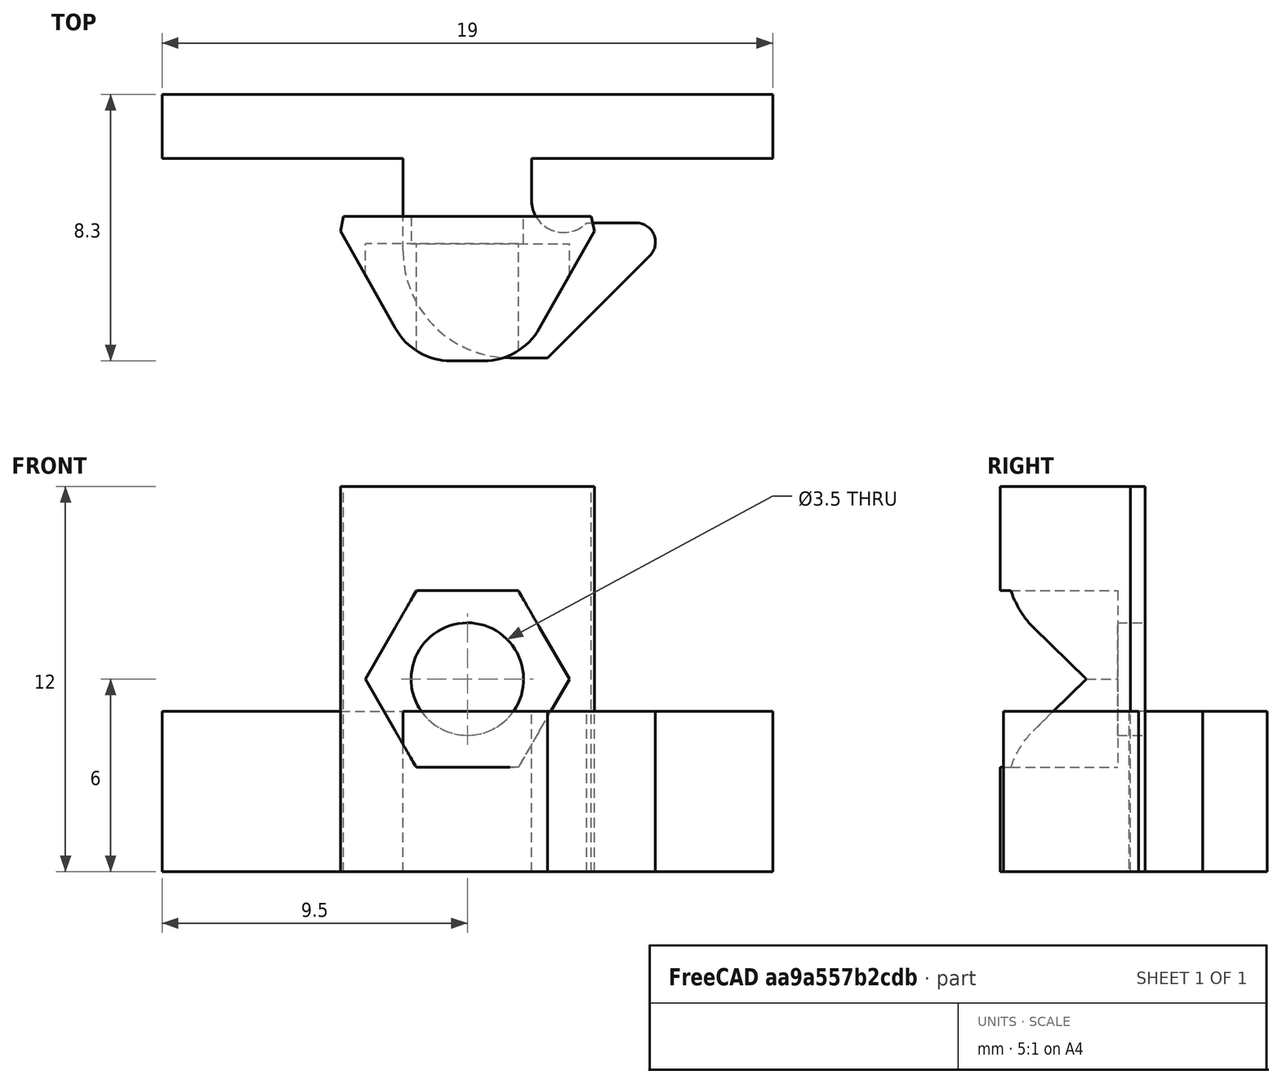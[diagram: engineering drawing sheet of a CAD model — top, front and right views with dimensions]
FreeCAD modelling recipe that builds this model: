
FCSTD DOCUMENT  (FreeCAD 0.18R)
Label: ISP5-3DP-T-Nut
Comment: Item Compatible Profile\nLook for ISP5-L20
License: All rights reserved
LicenseURL: http://en.wikipedia.org/wiki/All_rights_reserved
objects: Sketcher::SketchObject×6, PartDesign::Body×4, PartDesign::Pad×2, PartDesign::Pocket×2, Mesh::Feature×1
note: 18 computed .brp shape members not serialized (recipe doc carries the construction recipe); baked Part::Feature solids carry a one-line shape summary decoded from their .brp

FEATURE [Sketcher::SketchObject] CopySketch029  label="ISP5-L20-Profile"
  MapMode = 5
  sketch-geometry (70):
    g0: LineSegment StartX=-2.5 StartY=3.5 StartZ=0 EndX=-5.91967 EndY=6.91967 EndZ=0
    g1: LineSegment StartX=-5.38934 StartY=8.2 StartZ=0 EndX=-2.85 EndY=8.2 EndZ=0
    g2: LineSegment StartX=-3.35 StartY=10 StartZ=0 EndX=-8 EndY=10 EndZ=0
    g3: LineSegment StartX=-10 StartY=8 StartZ=0 EndX=-10 EndY=3.35 EndZ=0
    g4: LineSegment StartX=-9.25 StartY=2.6 StartZ=0 EndX=-8.45 EndY=2.6 EndZ=0
    g5: LineSegment StartX=-8.2 StartY=2.85 StartZ=0 EndX=-8.2 EndY=5.38934 EndZ=0
    g6: LineSegment StartX=-6.91967 StartY=5.91967 StartZ=0 EndX=-3.5 EndY=2.5 EndZ=0
    g7: LineSegment StartX=-2.6 StartY=9.25 StartZ=0 EndX=-2.6 EndY=8.45 EndZ=0
    g8: ArcOfCircle CenterX=-8 CenterY=8 CenterZ=0 NormalX=0 NormalY=0 NormalZ=1 AngleXU=0 Radius=2 StartAngle=1.5708 EndAngle=3.14159
    g9: ArcOfCircle CenterX=-3.35 CenterY=9.25 CenterZ=0 NormalX=0 NormalY=0 NormalZ=1 AngleXU=0 Radius=0.75 StartAngle=6e-16 EndAngle=1.5708
    g10: ArcOfCircle CenterX=-9.25 CenterY=3.35 CenterZ=0 NormalX=0 NormalY=0 NormalZ=1 AngleXU=0 Radius=0.75 StartAngle=3.14159 EndAngle=4.71239
    g11: ArcOfCircle CenterX=-5.38934 CenterY=7.45 CenterZ=0 NormalX=0 NormalY=0 NormalZ=1 AngleXU=0 Radius=0.75 StartAngle=1.5708 EndAngle=3.92699
    g12: ArcOfCircle CenterX=-7.45 CenterY=5.38934 CenterZ=0 NormalX=0 NormalY=0 NormalZ=1 AngleXU=0 Radius=0.75 StartAngle=0.785398 EndAngle=3.14159
    g13: LineSegment [constr] StartX=-5.38934 StartY=7.45 StartZ=0 EndX=-7.45 EndY=5.38934 EndZ=0
    g14: ArcOfCircle CenterX=-2.85 CenterY=8.45 CenterZ=0 NormalX=0 NormalY=0 NormalZ=1 AngleXU=0 Radius=0.25 StartAngle=4.71239 EndAngle=6.28319
    g15: Circle CenterX=0 CenterY=0 CenterZ=0 NormalX=0 NormalY=0 NormalZ=1 AngleXU=0 Radius=2.15
    g16: LineSegment StartX=2.5 StartY=3.5 StartZ=0 EndX=5.91967 EndY=6.91967 EndZ=0
    g17: LineSegment StartX=3.5 StartY=-2.5 StartZ=0 EndX=6.91967 EndY=-5.91967 EndZ=0
    g18: LineSegment StartX=2.5 StartY=-3.5 StartZ=0 EndX=5.91967 EndY=-6.91967 EndZ=0
    g19: LineSegment StartX=-2.5 StartY=-3.5 StartZ=0 EndX=-5.91967 EndY=-6.91967 EndZ=0
    g20: LineSegment StartX=-3.5 StartY=-2.5 StartZ=0 EndX=-6.91967 EndY=-5.91967 EndZ=0
    g21: LineSegment StartX=3.5 StartY=2.5 StartZ=0 EndX=6.91967 EndY=5.91967 EndZ=0
    g22: ArcOfCircle CenterX=-7.45 CenterY=-5.38934 CenterZ=0 NormalX=0 NormalY=0 NormalZ=1 AngleXU=0 Radius=0.75 StartAngle=3.14159 EndAngle=5.49779
    g23: ArcOfCircle CenterX=-5.38934 CenterY=-7.45 CenterZ=0 NormalX=0 NormalY=0 NormalZ=1 AngleXU=0 Radius=0.75 StartAngle=2.35619 EndAngle=4.71239
    g24: ArcOfCircle CenterX=5.38934 CenterY=-7.45 CenterZ=0 NormalX=0 NormalY=0 NormalZ=1 AngleXU=0 Radius=0.75 StartAngle=4.71239 EndAngle=7.06858
    g25: ArcOfCircle CenterX=7.45 CenterY=-5.38934 CenterZ=0 NormalX=0 NormalY=0 NormalZ=1 AngleXU=0 Radius=0.75 StartAngle=3.92699 EndAngle=6.28319
    g26: ArcOfCircle CenterX=5.38934 CenterY=7.45 CenterZ=0 NormalX=0 NormalY=0 NormalZ=1 AngleXU=0 Radius=0.75 StartAngle=5.49779 EndAngle=7.85398
    g27: ArcOfCircle CenterX=7.45 CenterY=5.38934 CenterZ=0 NormalX=0 NormalY=0 NormalZ=1 AngleXU=0 Radius=0.75 StartAngle=6e-16 EndAngle=2.35619
    g28: LineSegment StartX=-5.38934 StartY=-8.2 StartZ=0 EndX=-2.85 EndY=-8.2 EndZ=0
    g29: LineSegment StartX=2.85 StartY=-8.2 StartZ=0 EndX=5.38934 EndY=-8.2 EndZ=0
    g30: LineSegment StartX=8.2 StartY=-5.38934 StartZ=0 EndX=8.2 EndY=-2.85 EndZ=0
    g31: LineSegment StartX=8.2 StartY=5.38934 StartZ=0 EndX=8.2 EndY=2.85 EndZ=0
    g32: LineSegment StartX=5.38934 StartY=8.2 StartZ=0 EndX=2.85 EndY=8.2 EndZ=0
    g33: LineSegment StartX=-8.2 StartY=-5.38934 StartZ=0 EndX=-8.2 EndY=-2.85 EndZ=0
    g34: ArcOfCircle CenterX=-8.45 CenterY=-2.85 CenterZ=0 NormalX=0 NormalY=0 NormalZ=1 AngleXU=0 Radius=0.25 StartAngle=7e-16 EndAngle=1.5708
    g35: ArcOfCircle CenterX=-2.85 CenterY=-8.45 CenterZ=0 NormalX=0 NormalY=0 NormalZ=1 AngleXU=0 Radius=0.25 StartAngle=1e-15 EndAngle=1.5708
    g36: ArcOfCircle CenterX=2.85 CenterY=-8.45 CenterZ=0 NormalX=0 NormalY=0 NormalZ=1 AngleXU=0 Radius=0.25 StartAngle=1.5708 EndAngle=3.14159
    g37: ArcOfCircle CenterX=8.45 CenterY=-2.85 CenterZ=0 NormalX=0 NormalY=0 NormalZ=1 AngleXU=0 Radius=0.25 StartAngle=1.5708 EndAngle=3.14159
    g38: LineSegment StartX=2.6 StartY=9.25 StartZ=0 EndX=2.6 EndY=8.45 EndZ=0
    g39: LineSegment StartX=8.45 StartY=2.6 StartZ=0 EndX=9.25 EndY=2.6 EndZ=0
    g40: LineSegment StartX=8.45 StartY=-2.6 StartZ=0 EndX=9.25 EndY=-2.6 EndZ=0
    g41: LineSegment StartX=-8.45 StartY=-2.6 StartZ=0 EndX=-9.25 EndY=-2.6 EndZ=0
    g42: LineSegment StartX=-2.6 StartY=-8.45 StartZ=0 EndX=-2.6 EndY=-9.25 EndZ=0
    g43: LineSegment StartX=2.6 StartY=-8.45 StartZ=0 EndX=2.6 EndY=-9.25 EndZ=0
    g44: ArcOfCircle CenterX=8.45 CenterY=2.85 CenterZ=0 NormalX=0 NormalY=0 NormalZ=1 AngleXU=0 Radius=0.25 StartAngle=3.14159 EndAngle=4.71239
    g45: LineSegment StartX=3.35 StartY=10 StartZ=0 EndX=8 EndY=10 EndZ=0
    g46: ArcOfCircle CenterX=8 CenterY=8 CenterZ=0 NormalX=0 NormalY=0 NormalZ=1 AngleXU=0 Radius=2 StartAngle=2e-16 EndAngle=1.5708
    g47: LineSegment StartX=10 StartY=8 StartZ=0 EndX=10 EndY=3.35 EndZ=0
    g48: ArcOfCircle CenterX=9.25 CenterY=3.35 CenterZ=0 NormalX=0 NormalY=0 NormalZ=1 AngleXU=0 Radius=0.75 StartAngle=4.71239 EndAngle=6.28319
    g49: LineSegment StartX=3.35 StartY=-10 StartZ=0 EndX=8 EndY=-10 EndZ=0
    g50: ArcOfCircle CenterX=8 CenterY=-8 CenterZ=0 NormalX=0 NormalY=0 NormalZ=1 AngleXU=0 Radius=2 StartAngle=4.71239 EndAngle=6.28319
    g51: LineSegment StartX=10 StartY=-8 StartZ=0 EndX=10 EndY=-3.35 EndZ=0
    g52: ArcOfCircle CenterX=9.25 CenterY=-3.35 CenterZ=0 NormalX=0 NormalY=0 NormalZ=1 AngleXU=0 Radius=0.75 StartAngle=1e-16 EndAngle=1.5708
    g53: LineSegment StartX=-3.35 StartY=-10 StartZ=0 EndX=-8 EndY=-10 EndZ=0
    g54: LineSegment StartX=-10 StartY=-8 StartZ=0 EndX=-10 EndY=-3.35 EndZ=0
    g55: ArcOfCircle CenterX=-9.25 CenterY=-3.35 CenterZ=0 NormalX=0 NormalY=0 NormalZ=1 AngleXU=0 Radius=0.75 StartAngle=1.5708 EndAngle=3.14159
    g56: ArcOfCircle CenterX=-3.35 CenterY=-9.25 CenterZ=0 NormalX=0 NormalY=0 NormalZ=1 AngleXU=0 Radius=0.75 StartAngle=4.71239 EndAngle=6.28319
    g57: ArcOfCircle CenterX=3.35 CenterY=-9.25 CenterZ=0 NormalX=0 NormalY=0 NormalZ=1 AngleXU=0 Radius=0.75 StartAngle=3.14159 EndAngle=4.71239
    g58: ArcOfCircle CenterX=3.35 CenterY=9.25 CenterZ=0 NormalX=0 NormalY=0 NormalZ=1 AngleXU=0 Radius=0.75 StartAngle=1.5708 EndAngle=3.14159
    g59: ArcOfCircle CenterX=-8 CenterY=-8 CenterZ=0 NormalX=0 NormalY=0 NormalZ=1 AngleXU=0 Radius=2 StartAngle=3.14159 EndAngle=4.71239
    g60: ArcOfCircle CenterX=-8.45 CenterY=2.85 CenterZ=0 NormalX=0 NormalY=0 NormalZ=1 AngleXU=0 Radius=0.25 StartAngle=4.71239 EndAngle=6.28319
    g61: ArcOfCircle CenterX=2.85 CenterY=8.45 CenterZ=0 NormalX=0 NormalY=0 NormalZ=1 AngleXU=0 Radius=0.25 StartAngle=3.14159 EndAngle=4.71239
    g62: LineSegment StartX=0 StartY=3.5 StartZ=0 EndX=2.5 EndY=3.5 EndZ=0
    g63: LineSegment StartX=0 StartY=3.5 StartZ=0 EndX=-2.5 EndY=3.5 EndZ=0
    g64: LineSegment StartX=-3.5 StartY=2.5 StartZ=0 EndX=-3.5 EndY=0 EndZ=0
    g65: LineSegment StartX=-3.5 StartY=0 StartZ=0 EndX=-3.5 EndY=-2.5 EndZ=0
    g66: LineSegment StartX=-2.5 StartY=-3.5 StartZ=0 EndX=0 EndY=-3.5 EndZ=0
    g67: LineSegment StartX=0 StartY=-3.5 StartZ=0 EndX=2.5 EndY=-3.5 EndZ=0
    g68: LineSegment StartX=3.5 StartY=-2.5 StartZ=0 EndX=3.5 EndY=0 EndZ=0
    g69: LineSegment StartX=3.5 StartY=0 StartZ=0 EndX=3.5 EndY=2.5 EndZ=0
  constraints (173):
    c: Vertical(g7)
    c: Horizontal(g1)
    c: Vertical(g5)
    c: Horizontal(g4)
    c: Coincident(g2,g9)
    c: Coincident(g9,g7)
    c: Radius(g9) = 0.75
    c: DistanceY(g1,g2) = 1.8
    c: Coincident(g3,g10)
    c: Coincident(g10,g4)
    c: Radius(g10) = 0.75
    c: Horizontal(g9,g7)
    c: Vertical(g2,g9)
    c: Coincident(g0,g11)
    c: Coincident(g11,g1)
    c: Vertical(g1,g11)
    c: Radius(g11) = 0.75
    c: Coincident(g12,g6)
    c: Coincident(g12,g5)
    c: Equal(g11,g12)
    c: Horizontal(g5,g12)
    c: Coincident(g12,g13)
    c: Coincident(g11,g13)
    c: PointOnObject(g0,g13)
    c: PointOnObject(g6,g13)
    c: Horizontal(g3,g10)
    c: Vertical(g10,g4)
    c: Horizontal(g2)
    c: Vertical(g3)
    c: Parallel(g6,g0)
    c: Tangent(g2,g8) = -1.5708
    c: Tangent(g3,g8) = -1.5708
    c: Radius(g8) = 2
    c: Perpendicular(g13,g6)
    c: Coincident(g7,g14)
    c: Coincident(g1,g14)
    c: Vertical(g14,g1)
    c: Horizontal(g14,g7)
    c: Radius(g14) = 0.25
    c: DistanceX(g3,g5) = 1.8
    c: Coincident(g15,g-1)
    c: Radius(g15) = 2.15
    c: DistanceX(g0,g16) = 5
    c: Symmetric(g16,g0,g-2)
    c: Symmetric(g21,g6,g-2)
    c: Equal(g16,g21)
    c: Parallel(g20,g19)
    c: Parallel(g18,g17)
    c: Symmetric(g6,g20,g-1)
    c: Symmetric(g0,g19,g-1)
    c: Tangent(g16,g26) = -1.5708
    c: Tangent(g21,g27) = 1.5708
    c: Tangent(g17,g25) = -1.5708
    c: Tangent(g18,g24) = 1.5708
    c: Tangent(g19,g23) = -1.5708
    c: Tangent(g20,g22) = 1.5708
    c: Horizontal(g28)
    c: Tangent(g26,g32) = -1.5708
    c: Tangent(g27,g31) = 1.5708
    c: Tangent(g25,g30) = -1.5708
    c: Tangent(g24,g29) = -1.5708
    c: Tangent(g23,g28) = -1.5708
    c: Tangent(g22,g33) = 1.5708
    c: Tangent(g30,g37) = 1.5708
    c: Tangent(g36,g29) = 1.5708
    c: Tangent(g28,g35) = 1.5708
    c: Tangent(g34,g33) = -1.5708
    c: Symmetric(g0,g16,g-2)
    c: Symmetric(g21,g17,g-1)
    c: Symmetric(g18,g19,g-2)
    c: Symmetric(g6,g20,g-1)
    c: Symmetric(g23,g1,g-1)
    c: Symmetric(g24,g26,g-1)
    c: DistanceX(g6,g21) = 7
    c: Vertical(g42)
    c: Vertical(g43)
    c: Tangent(g44,g31) = -1.5708
    c: Tangent(g44,g39) = -1.5708
    c: Tangent(g37,g40) = 1.5708
    c: Tangent(g36,g43) = -1.5708
    c: Tangent(g35,g42) = 1.5708
    c: Tangent(g41,g34) = -1.5708
    c: Symmetric(g5,g27,g-2)
    c: Symmetric(g22,g25,g-2)
    c: Vertical(g7,g35)
    c: Symmetric(g4,g41,g-1)
    c: Symmetric(g7,g38,g-2)
    c: Symmetric(g39,g40,g-1)
    c: Tangent(g45,g46) = 1.5708
    c: Tangent(g46,g47) = 1.5708
    c: Tangent(g47,g48) = 1.5708
    c: Tangent(g49,g50) = -1.5708
    c: Tangent(g50,g51) = -1.5708
    c: Tangent(g51,g52) = -1.5708
    c: Tangent(g54,g55) = 1.5708
    c: Tangent(g55,g41) = -1.5708
    c: Tangent(g40,g52) = 1.5708
    c: Tangent(g48,g39) = -1.5708
    c: Vertical(g51)
    c: Vertical(g47)
    c: Horizontal(g45)
    c: Horizontal(g49)
    c: Horizontal(g53)
    c: Tangent(g45,g58) = 1.5708
    c: Tangent(g38,g58) = -1.5708
    c: Tangent(g43,g57) = -1.5708
    c: Tangent(g49,g57) = -1.5708
    c: Tangent(g53,g56) = 1.5708
    c: Tangent(g42,g56) = 1.5708
    c: DistanceX(g3,g46) = 20
    c: Tangent(g54,g59) = 1.5708
    c: Tangent(g53,g59) = 1.5708
    c: DistanceY(g53,g2) = 20
    c: Symmetric(g54,g51,g-2)
    c: Vertical(g51,g47)
    c: Horizontal(g39)
    c: Horizontal(g40)
    c: Vertical(g54)
    c: DistanceX(g7,g38) = 5.2
    c: DistanceY(g41,g4) = 5.2
    c: DistanceY(g40,g39) = 5.2
    c: Horizontal(g2,g45)
    c: Vertical(g3,g54)
    c: Horizontal(g53,g49)
    c: Vertical(g38)
    c: Horizontal(g32)
    c: Vertical(g30)
    c: Vertical(g31)
    c: Vertical(g33)
    c: Vertical(g5,g33)
    c: Horizontal(g41)
    c: Radius(g46) = 2
    c: Radius(g50) = 2
    c: Radius(g59) = 2
    c: Radius(g56) = 0.75
    c: Symmetric(g42,g43,g-2)
    c: Radius(g35) = 0.25
    c: Radius(g44) = 0.25
    c: Radius(g34) = 0.25
    c: Radius(g37) = 0.25
    c: Tangent(g5,g60) = -1.5708
    c: Tangent(g4,g60) = -1.5708
    c: Radius(g60) = 0.25
    c: Tangent(g61,g38) = -1.5708
    c: Tangent(g32,g61) = 1.5708
    c: Radius(g61) = 0.25
    c: Radius(g36) = 0.25
    c: Horizontal(g1,g32)
    c: Coincident(g62,g63)
    c: Horizontal(g63)
    c: PointOnObject(g62,g-2)
    c: Coincident(g16,g62)
    c: Coincident(g0,g63)
    c: Coincident(g68,g69)
    c: Coincident(g66,g67)
    c: Coincident(g64,g65)
    c: Coincident(g20,g65)
    c: Coincident(g19,g66)
    c: Coincident(g18,g67)
    c: Coincident(g17,g68)
    c: Coincident(g21,g69)
    c: Coincident(g6,g64)
    c: PointOnObject(g64,g-1)
    c: PointOnObject(g68,g-1)
    c: PointOnObject(g66,g-2)
    c: Vertical(g64)
    c: Horizontal(g66)
    c: Horizontal(g67)
    c: Vertical(g69)
    c: Vertical(g68)
    c: DistanceY(g20,g6) = 5
    c: DistanceY(g19,g0) = 7
    c: Vertical(g16,g18)
FEATURE [PartDesign::Body] Body  label="Extrusion"
  Group = -> [CopySketch029]
  Origin = -> Origin
FEATURE [Sketcher::SketchObject] Sketch  label="T-Nut-Base-Profile"
  MapMode = 5
  Support = -> [XY_Plane001]
  sketch-geometry (8):
    g0: LineSegment StartX=-3.85 StartY=8.2 StartZ=0 EndX=3.85 EndY=8.2 EndZ=0
    g1: LineSegment StartX=3.95 StartY=7.75 StartZ=0 EndX=2.24262 EndY=4.71853 EndZ=0
    g2: ArcOfCircle CenterX=0.5 CenterY=5.7 CenterZ=0 NormalX=0 NormalY=0 NormalZ=1 AngleXU=0 Radius=2 StartAngle=4.71239 EndAngle=5.77025
    g3: LineSegment StartX=0.5 StartY=3.7 StartZ=0 EndX=-0.5 EndY=3.7 EndZ=0
    g4: ArcOfCircle CenterX=-0.5 CenterY=5.7 CenterZ=0 NormalX=0 NormalY=0 NormalZ=1 AngleXU=0 Radius=2 StartAngle=3.65453 EndAngle=4.71239
    g5: LineSegment StartX=-2.24262 StartY=4.71853 StartZ=0 EndX=-3.95 EndY=7.75 EndZ=0
    g6: LineSegment StartX=-3.85 StartY=8.2 StartZ=0 EndX=-3.95 EndY=7.75 EndZ=0
    g7: LineSegment StartX=3.85 StartY=8.2 StartZ=0 EndX=3.95 EndY=7.75 EndZ=0
  constraints (19):
    c: Tangent(g1,g2) = 1.5708
    c: Tangent(g2,g3) = 1.5708
    c: Tangent(g3,g4) = 1.5708
    c: Tangent(g4,g5) = 1.5708
    c: DistanceX(g3,g3) = 1
    c: Symmetric(g2,g3,g-2)
    c: Symmetric(g4,g1,g-2)
    c: DistanceY(g3,g0) = 4.5
    c: Radius(g4) = 2
    c: DistanceY(g-1,g0) = 8.2
    c: DistanceX(g0,g0) = 7.7
    c: Symmetric(g0,g0,g-2)
    c: Coincident(g1,g7)
    c: Coincident(g0,g7)
    c: Coincident(g0,g6)
    c: Coincident(g5,g6)
    c: DistanceY(g1,g0) = 0.45
    c: DistanceX(g5,g1) = 7.9
    c: Horizontal(g5,g1)
FEATURE [PartDesign::Pad] Pad  label="NutBody"
  Length = 12
  Length2 = 100
  Profile = -> Sketch
  Type = 0
FEATURE [Sketcher::SketchObject] Sketch001  label="M3HexProfile"
  MapMode = 5
  Placement = pos=(0,3.7,0) rot=(1,0,0;1.5708rad)
  Support = -> [Pad]
  sketch-geometry (7):
    g0: LineSegment StartX=-3.17543 StartY=6 StartZ=0 EndX=-1.58771 EndY=3.25 EndZ=0
    g1: LineSegment StartX=-1.58771 StartY=3.25 StartZ=0 EndX=1.58771 EndY=3.25 EndZ=0
    g2: LineSegment StartX=1.58771 StartY=3.25 StartZ=0 EndX=3.17543 EndY=6 EndZ=0
    g3: LineSegment StartX=3.17543 StartY=6 StartZ=0 EndX=1.58771 EndY=8.75 EndZ=0
    g4: LineSegment StartX=1.58771 StartY=8.75 StartZ=0 EndX=-1.58771 EndY=8.75 EndZ=0
    g5: LineSegment StartX=-1.58771 StartY=8.75 StartZ=0 EndX=-3.17543 EndY=6 EndZ=0
    g6: Circle [constr] CenterX=0 CenterY=6 CenterZ=0 NormalX=0 NormalY=0 NormalZ=1 AngleXU=0 Radius=3.17543
  constraints (17):
    c: Coincident(g0,g1)
    c: Coincident(g1,g2)
    c: Coincident(g2,g3)
    c: Coincident(g3,g4)
    c: Coincident(g4,g5)
    c: Coincident(g5,g0)
    c: Equal(g0, g1-g5) x5
    c: PointOnObject(g0,g6)
    c: PointOnObject(g1,g6)
    c: PointOnObject(g2,g6)
    c: PointOnObject(g3,g6)
    c: PointOnObject(g4,g6)
    c: PointOnObject(g5,g6)
    c: Horizontal(g0,g2)
    c: PointOnObject(g6,g-2)
    c: DistanceY(g-1,g6) = 6
    c: Distance(g4,g2) = 5.5
FEATURE [PartDesign::Pocket] Pocket  label="M3Hole"
  BaseFeature = -> Pad
  Length = 3.65
  Length2 = 100
  Profile = -> Sketch001
  Type = 0
FEATURE [Sketcher::SketchObject] Sketch002  label="M3ShaftProfile"
  MapMode = 5
  Placement = pos=(0,8.2,0) rot=(0,0.707107,0.707107;3.14159rad)
  Support = -> [Pocket]
  sketch-geometry (1):
    g0: Circle CenterX=0 CenterY=6 CenterZ=0 NormalX=0 NormalY=0 NormalZ=1 AngleXU=0 Radius=1.75
  constraints (3):
    c: PointOnObject(g0,g-2)
    c: DistanceY(g-1,g0) = 6
    c: Radius(g0) = 1.75
FEATURE [PartDesign::Pocket] Pocket001  label="M3ShaftHole"
  BaseFeature = -> Pocket
  Length = 5
  Length2 = 100
  Profile = -> Sketch002
  Type = 0
FEATURE [PartDesign::Body] Body001  label="T-Nut"
  Group = -> [Sketch,Pad,Sketch001,Pocket,Sketch002,Pocket001]
  Origin = -> Origin001
  Tip = -> Pocket001
FEATURE [Mesh::Feature] Mesh  label="T-Nut (Meshed)"
  Placement = pos=(0,0,0) rot=(1,0,0;4.71239rad)
FEATURE [Sketcher::SketchObject] Sketch003
  MapMode = 5
  Support = -> [XY_Plane002]
  sketch-geometry (11):
    g0: LineSegment StartX=5 StartY=8 StartZ=0 EndX=5 EndY=6.5 EndZ=0
    g1: LineSegment StartX=5 StartY=6.5 StartZ=0 EndX=2.5 EndY=4 EndZ=0
    g2: LineSegment StartX=2.5 StartY=4 StartZ=0 EndX=0 EndY=4 EndZ=0
    g3: LineSegment StartX=0 StartY=4 StartZ=0 EndX=0 EndY=10 EndZ=0
    g4: LineSegment StartX=0 StartY=10 StartZ=0 EndX=-9.5 EndY=10 EndZ=0
    g5: LineSegment StartX=-9.5 StartY=10 StartZ=0 EndX=-9.5 EndY=12 EndZ=0
    g6: LineSegment StartX=-9.5 StartY=12 StartZ=0 EndX=9.5 EndY=12 EndZ=0
    g7: LineSegment StartX=9.5 StartY=12 StartZ=0 EndX=9.5 EndY=10 EndZ=0
    g8: LineSegment StartX=9.5 StartY=10 StartZ=0 EndX=2.5 EndY=10 EndZ=0
    g9: LineSegment StartX=2.5 StartY=10 StartZ=0 EndX=2.5 EndY=8 EndZ=0
    g10: LineSegment StartX=2.5 StartY=8 StartZ=0 EndX=5 EndY=8 EndZ=0
  constraints (32):
    c: Coincident(g0,g1)
    c: Coincident(g1,g2)
    c: Coincident(g2,g3)
    c: Coincident(g3,g4)
    c: Coincident(g4,g5)
    c: Coincident(g5,g6)
    c: Coincident(g6,g7)
    c: Coincident(g7,g8)
    c: Coincident(g8,g9)
    c: Coincident(g9,g10)
    c: Coincident(g10,g0)
    c: Vertical(g0)
    c: Vertical(g3)
    c: Vertical(g5)
    c: Vertical(g7)
    c: Horizontal(g4)
    c: Horizontal(g8)
    c: Horizontal(g10)
    c: Horizontal(g2)
    c: Vertical(g9)
    c: DistanceX(g3,g0) = 5
    c: Symmetric(g6,g5,g-2)
    c: DistanceX(g6,g6) = 19
    c: DistanceX(g3,g8) = 2.5
    c: PointOnObject(g3,g-2)
    c: Angle(g-1,g1) = 0.785398
    c: DistanceY(g3,g3) = 6
    c: DistanceY(g5,g5) = 2
    c: DistanceY(g-1,g3) = 10
    c: Horizontal(g3,g8)
    c: DistanceY(g9,g9) = 2
    c: DistanceX(g2,g2) = 2.5
FEATURE [PartDesign::Body] Body002  label="ISP5-Clamp-Flat"
  Group = -> [Sketch003]
  Origin = -> Origin002
FEATURE [Sketcher::SketchObject] Sketch004
  MapMode = 5
  Support = -> [XY_Plane003]
  sketch-geometry (13):
    g0: LineSegment StartX=5.67574 StartY=6.97574 StartZ=0 EndX=2.5 EndY=3.8 EndZ=0
    g1: LineSegment StartX=2.5 StartY=3.8 StartZ=0 EndX=1.33 EndY=3.8 EndZ=0
    g2: LineSegment StartX=-9.5 StartY=10 StartZ=0 EndX=-9.5 EndY=12 EndZ=0
    g3: LineSegment StartX=-9.5 StartY=12 StartZ=0 EndX=9.5 EndY=12 EndZ=0
    g4: LineSegment StartX=9.5 StartY=12 StartZ=0 EndX=9.5 EndY=10 EndZ=0
    g5: LineSegment StartX=9.5 StartY=10 StartZ=0 EndX=2 EndY=10 EndZ=0
    g6: LineSegment StartX=2 StartY=10 StartZ=0 EndX=2 EndY=8.7 EndZ=0
    g7: LineSegment StartX=3.71414 StartY=8 StartZ=0 EndX=5.25147 EndY=8 EndZ=0
    g8: ArcOfCircle CenterX=1.33 CenterY=7.13 CenterZ=0 NormalX=0 NormalY=0 NormalZ=1 AngleXU=0 Radius=3.33 StartAngle=3.14159 EndAngle=4.71239
    g9: LineSegment StartX=-9.5 StartY=10 StartZ=0 EndX=-2 EndY=10 EndZ=0
    g10: LineSegment StartX=-2 StartY=7.13 StartZ=0 EndX=-2 EndY=10 EndZ=0
    g11: ArcOfCircle CenterX=3 CenterY=8.7 CenterZ=0 NormalX=0 NormalY=0 NormalZ=1 AngleXU=0 Radius=1 StartAngle=3.14159 EndAngle=5.50779
    g12: ArcOfCircle CenterX=5.25147 CenterY=7.4 CenterZ=0 NormalX=0 NormalY=0 NormalZ=1 AngleXU=0 Radius=0.6 StartAngle=5.49779 EndAngle=7.85398
  constraints (35):
    c: Coincident(g0,g1)
    c: Coincident(g2,g3)
    c: Coincident(g3,g4)
    c: Coincident(g4,g5)
    c: Coincident(g5,g6)
    c: Vertical(g2)
    c: Vertical(g4)
    c: Horizontal(g5)
    c: Horizontal(g7)
    c: Horizontal(g1)
    c: Vertical(g6)
    c: Symmetric(g3,g2,g-2)
    c: DistanceX(g3,g3) = 19
    c: Angle(g-1,g0) = 0.785398
    c: DistanceY(g2,g2) = 2
    c: Horizontal(g9)
    c: Coincident(g2,g9)
    c: Coincident(g9,g10)
    c: Vertical(g10)
    c: Tangent(g8,g10) = 1.5708
    c: Coincident(g7,g11)
    c: Tangent(g8,g1) = 1.5708
    c: DistanceY(g-1,g2) = 10
    c: Tangent(g6,g11) = -1.5708
    c: Tangent(g0,g12) = 1.5708
    c: Tangent(g7,g12) = 1.5708
    c: DistanceX(g9,g5) = 4
    c: Radius(g8) = 3.33
    c: Radius(g11) = 1
    c: Radius(g12) = 0.6
    c: Symmetric(g9,g5,g-2)
    c: DistanceY(g0,g5) = 6.2
    c: DistanceX(g-1,g0) = 2.5
    c: DistanceY(g7,g5) = 2
    c: DistanceY(g6,g5) = 1.3
FEATURE [PartDesign::Pad] Pad001
  Length = 5
  Length2 = 100
  Profile = -> Sketch004
  Type = 0
FEATURE [PartDesign::Body] Body003  label="ISP5-Clamp-Roll"
  Group = -> [Sketch004,Pad001]
  Origin = -> Origin003
  Tip = -> Pad001
